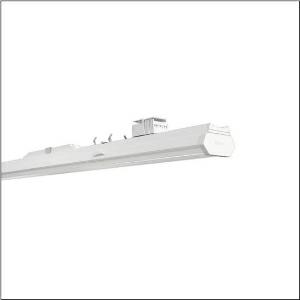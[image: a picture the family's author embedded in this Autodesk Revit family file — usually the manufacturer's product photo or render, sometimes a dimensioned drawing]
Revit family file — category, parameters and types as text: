
# Revit family: licross_r__21_protected_ho_52td13cn4c5s_0d58
name_source: partatom
category: Lighting Fixtures
units: mm (PartAtom-declared; Revit-internal decimal feet)

## family parameters
Cut with Voids When Loaded = No
Host = Face
Light Source = No
Part Type = Normal
Room Calculation Point = No
Round Connector Dimension = Use Diameter
Shared = No

## types (1)
- --- (1 x LED, 12680 lm, 68.9 W, 4000K)
    Apparent Load = 69 VA
    CIE Flux Codes = 89 96 99 100 99
    Color Rendering = 80
    Color Temperature = 4000K
    Default Elevation = 1800 mm
    Description = Licross® 21 Protected HO, luminaire insert, of sheet steel, galvanised, coil coated, white, length: 1.500mm, width: 66mm, height: 67mm, LED rated luminous flux: 12.690lm, light colour: 840, control gear: ON/OFF Multilumen, CLOi, control gear: ECG Multilumen, with plug, 3-pole, with phase selection, mains connection: 220..240V, AC, 50/60Hz, start of lifetime: 69W, end of service life: 83W, internal wiring halogen-free, primary light control with lens, of plastic, primary optical cover: cover, of PMMA, light emission: direct distribution, primary light characteristic: symmetric, protection rating (complete): IP54, insulation class (complete): insulation class I (protective earthing), certification: CE, ENEC, VDE, UKCA, protection symbol: D if used in an environment with non-conductive dust loads with corresponding accessories, impact resistance: IK06, permissible ambient temperature for indoor applications: -35..+35°C, corresponds to IFS (International Featured Standards) requirements for safety and quality in the food industry, reducing of maximum allowable ambient temperature of 5°C with ceiling mounting, LABS conformity tested according to VDMA 24364:2018-05, packaging unit: 1 piece
    Height = 92 mm
    Lamp = 1 x LED
    Lamp Light Flux = 12680 lm
    Lamp Power = 68.9 W
    Lamp count = 1
    Length = 1500 mm
    Luminous efficacy = 184 lm/W
    Manufacturer = Siteco
    ModVariant = No
    Model = 52TD13CN4C5S
    Mounting Place = Ceiling
    Mounting Type = Pendant
    Number of Poles = 1
    OnlyDefault = Yes
    Power Factor = 1
    Product Name = Licross® 21 Protected HO
    Product group = luminaire insert | ceiling pendant
    ProductGroupID = 902
    Protection Class = Protection class I
    Protection Degree = IP 54
    RLX_Detail_Level = 1
    RLX_Emergency_Light_Flux = 0 lm
    RLX_Emergency_Type = 0
    RLX_Emergency_Type_DB = No
    RlxData = <blob elided: 22109 chars, md5=75546c20>
    Socket = socket
    Standby Power = 0 W
    System Light Flux = 12680 lm
    System Power = 69 W
    Type Comments = factory setting: luminous flux: 100 % | (A | C | E) | 162 mA
    Type Image = l_1256148.jpg
    URL = http://relux.com
    VarID = @adj_132323
    Voltage = 0 V
    Weight = 0.00 kg
    Width = 88 mm

## geometry (parser evidence)
native form markers: Blend x4, Sweep x10
no freeform markers — native parametric forms only
